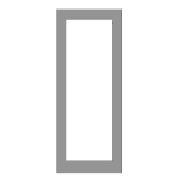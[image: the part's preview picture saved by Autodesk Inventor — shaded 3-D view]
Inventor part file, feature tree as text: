
AUTODESK INVENTOR PART (.ipt)
format: ipt  version: 2020 (Build 240168000, 168)  size: 130,560 bytes
history: native  units: in
note: dims shown in document units (in); Inventor stores cm internally (conversion verified against a paired STEP export)
features: other x4, plane x3, sketch x3, split x2
ambient origin geometry x8: Origin, YZ Plane, XZ Plane, XY Plane, X Axis, Y Axis, Z Axis, Center Point
bodies: Solid1 (feature_tree), Body (feature_tree)
feature tree (12):
  other  "Driven Length"
  other  "Frame Generator"
  other  "Start Plane"
  other  "End Plane"
  plane  "Work Plane6"
  split  "Split1"
  plane  "Work Plane7"
  split  "Split2"
  sketch  "Sketch"  dims[d2=0.125in d3=0.125in d6=0.5in d7=24.5in d8=0.13in d9=0.0in d14=90.0deg d11=24.0in]
  sketch  "Sketch6"  dims[d0=1.0in]
  plane  "Work Plane5"
  sketch  "Sketch7"  dims[d1=3.0in]
